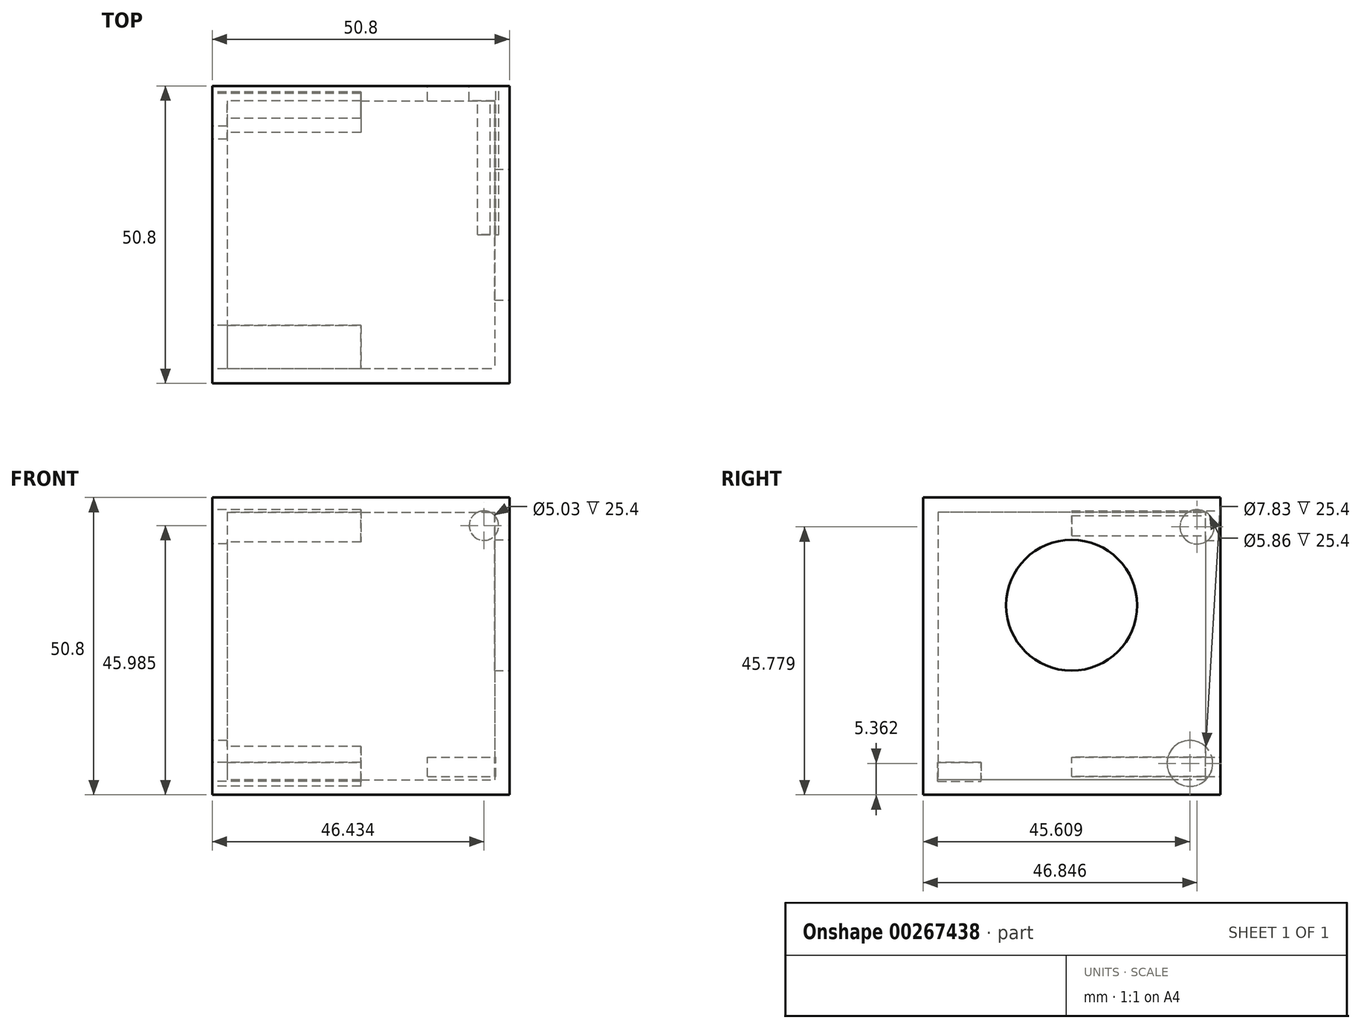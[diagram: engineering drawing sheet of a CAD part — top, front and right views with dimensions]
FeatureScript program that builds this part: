
annotation { "Feature Type Name" : "Feature", "Feature Type Description" : "" }
export const myFeature = defineFeature(function(context is Context, id is Id, definition is map)
    precondition{}
    {
        {
            var Q0;
            Q0=qCreatedBy(makeId("Top.planeOp"),FACE);
            var sketch = newSketch(context, id + "F0", { "sketchPlane" : qUnion([Q0])});
            skLineSegment(sketch, "E0.bottom", {"start": v(-25.4, 25.4) * mm, "end": v(25.4, 25.4) * mm});
            skLineSegment(sketch, "E0.top", {"start": v(-25.4, -25.4) * mm, "end": v(25.4, -25.4) * mm});
            skLineSegment(sketch, "E0.left", {"start": v(-25.4, 25.4) * mm, "end": v(-25.4, -25.4) * mm});
            skLineSegment(sketch, "E0.right", {"start": v(25.4, 25.4) * mm, "end": v(25.4, -25.4) * mm});
            skPoint(sketch, "E0.middle", {"position": v(0, 0) * mm});
            skSolve(sketch);
        }
        {
            var Q0;
            Q0=makeQuery(id+"F0.imprint","IMPRINT",FACE,{"disambiguationData":[TD([[makeQuery(id+"F0.imprint","IMPRINT",EDGE,{"derivedFrom":sQuery(id+"F0.wireOp",EDGE,"E0.bottom")}),-1.0]])]});
            extrude(context, id + "F1", {"entities" : qUnion([Q0]), "depth" : 50.8 * mm});
        }
        {
            var Q0;
            Q0=makeQuery(id+"F1.opExtrude","SWEPT_FACE",FACE,{"disambiguationData":[OSD([sQuery(id+"F0.wireOp",EDGE,"E0.right")])]});
            var sketch = newSketch(context, id + "F2", { "sketchPlane" : qUnion([Q0])});
            skCircle(sketch, "E1", {"center": v(0, 32.38) * mm, "radius": 11.19 * mm});
            skSolve(sketch);
        }
        {
            var Q0;
            Q0=makeQuery(id+"F1.opExtrude","CAP_FACE",FACE,{"disambiguationData":[OSD([sQuery(id+"F0.wireOp",EDGE,"E0.bottom"),sQuery(id+"F0.wireOp",EDGE,"E0.top"),sQuery(id+"F0.wireOp",EDGE,"E0.left"),sQuery(id+"F0.wireOp",EDGE,"E0.right")])],"isStart":false});
            var Q1;
            Q1=makeQuery(id+"F1.opExtrude","SWEPT_BODY",BODY,{"disambiguationData":[OSD([sQuery(id+"F0.wireOp",EDGE,"E0.bottom"),sQuery(id+"F0.wireOp",EDGE,"E0.top"),sQuery(id+"F0.wireOp",EDGE,"E0.left"),sQuery(id+"F0.wireOp",EDGE,"E0.right")])]});
            shell(context, id + "F3", {"isHollow" : true, "entities" : qUnion([Q0]), "parts" : qUnion([Q1]), "thickness" : 2.54 * mm});
        }
        {
            var Q0;
            Q0=makeQuery(id+"F2.imprint","IMPRINT",FACE,{"disambiguationData":[TD([[makeQuery(id+"F2.imprint","IMPRINT",EDGE,{"derivedFrom":sQuery(id+"F2.wireOp",EDGE,"E1")}),1.0]])]});
            var Q1;
            Q1=sQuery(id+"F2.wireOp",EDGE,"E1");
            extrude(context, id + "F4", {"entities" : qUnion([Q0]), "operationType" : NewBodyOperationType.REMOVE, "surfaceEntities" : qUnion([Q1]), "endBound" : BoundingType.UP_TO_NEXT, "oppositeDirection" : true, "depth" : 25.4 * mm});
        }
        {
            var Q0;
            Q0=makeQuery(id+"F1.opExtrude","SWEPT_FACE",FACE,{"disambiguationData":[OSD([sQuery(id+"F0.wireOp",EDGE,"E0.bottom")])]});
            var sketch = newSketch(context, id + "F5", { "sketchPlane" : qUnion([Q0])});
            skLineSegment(sketch, "E2.bottom", {"start": v(-11.4, 3.1) * mm, "end": v(-23.07, 3.1) * mm});
            skLineSegment(sketch, "E2.top", {"start": v(-11.4, 6.4) * mm, "end": v(-23.07, 6.4) * mm});
            skLineSegment(sketch, "E2.left", {"start": v(-11.4, 3.1) * mm, "end": v(-11.4, 6.4) * mm});
            skLineSegment(sketch, "E2.right", {"start": v(-23.07, 3.1) * mm, "end": v(-23.07, 6.4) * mm});
            skPoint(sketch, "E2.middle", {"position": v(-17.23, 4.74) * mm});
            skSolve(sketch);
        }
        {
            var Q0;
            Q0=makeQuery(id+"F5.imprint","IMPRINT",FACE,{"disambiguationData":[TD([[makeQuery(id+"F5.imprint","IMPRINT",EDGE,{"derivedFrom":sQuery(id+"F5.wireOp",EDGE,"E2.bottom")}),-1.0]])]});
            extrude(context, id + "F6", {"entities" : qUnion([Q0]), "operationType" : NewBodyOperationType.REMOVE, "oppositeDirection" : true, "depth" : 25.4 * mm});
        }
        {
            var Q0;
            Q0=makeQuery(id+"F1.opExtrude","SWEPT_FACE",FACE,{"disambiguationData":[OSD([sQuery(id+"F0.wireOp",EDGE,"E0.bottom")])]});
            var sketch = newSketch(context, id + "F7", { "sketchPlane" : qUnion([Q0])});
            skCircle(sketch, "E3", {"center": v(-21.03, 45.99) * mm, "radius": 2.52 * mm});
            skCircle(sketch, "E4", {"center": v(20.41, 5.16) * mm, "radius": 3.85 * mm});
            skSolve(sketch);
        }
        {
            var Q0;
            Q0=makeQuery(id+"F7.imprint","IMPRINT",FACE,{"disambiguationData":[TD([[makeQuery(id+"F7.imprint","IMPRINT",EDGE,{"derivedFrom":sQuery(id+"F7.wireOp",EDGE,"E3")}),1.0]])]});
            extrude(context, id + "F8", {"entities" : qUnion([Q0]), "operationType" : NewBodyOperationType.REMOVE, "oppositeDirection" : true, "depth" : 25.4 * mm});
        }
        {
            var Q0;
            Q0=makeQuery(id+"F1.opExtrude","SWEPT_FACE",FACE,{"disambiguationData":[OSD([sQuery(id+"F0.wireOp",EDGE,"E0.left")])]});
            var sketch = newSketch(context, id + "F9", { "sketchPlane" : qUnion([Q0])});
            skCircle(sketch, "E5", {"center": v(-21.45, 45.78) * mm, "radius": 2.93 * mm});
            skCircle(sketch, "E6", {"center": v(-20.2, 5.36) * mm, "radius": 3.91 * mm});
            skLineSegment(sketch, "E7.bottom", {"start": v(22.89, 2.27) * mm, "end": v(15.46, 2.27) * mm});
            skLineSegment(sketch, "E7.top", {"start": v(22.89, 5.57) * mm, "end": v(15.46, 5.57) * mm});
            skLineSegment(sketch, "E7.left", {"start": v(22.89, 2.27) * mm, "end": v(22.89, 5.57) * mm});
            skLineSegment(sketch, "E7.right", {"start": v(15.46, 2.27) * mm, "end": v(15.46, 5.57) * mm});
            skPoint(sketch, "E7.middle", {"position": v(19.18, 3.92) * mm});
            skSolve(sketch);
        }
        {
            var Q0;
            Q0=makeQuery(id+"F9.imprint","IMPRINT",FACE,{"disambiguationData":[TD([[makeQuery(id+"F9.imprint","IMPRINT",EDGE,{"derivedFrom":sQuery(id+"F9.wireOp",EDGE,"E5")}),1.0]])]});
            var Q1;
            Q1=makeQuery(id+"F9.imprint","IMPRINT",FACE,{"disambiguationData":[TD([[makeQuery(id+"F9.imprint","IMPRINT",EDGE,{"derivedFrom":sQuery(id+"F9.wireOp",EDGE,"E6")}),1.0]])]});
            var Q2;
            Q2=makeQuery(id+"F9.imprint","IMPRINT",FACE,{"disambiguationData":[TD([[makeQuery(id+"F9.imprint","IMPRINT",EDGE,{"derivedFrom":sQuery(id+"F9.wireOp",EDGE,"E7.bottom")}),-1.0]])]});
            extrude(context, id + "F10", {"entities" : qUnion([Q0, Q1, Q2]), "operationType" : NewBodyOperationType.REMOVE, "oppositeDirection" : true, "depth" : 25.4 * mm});
        }
    });
